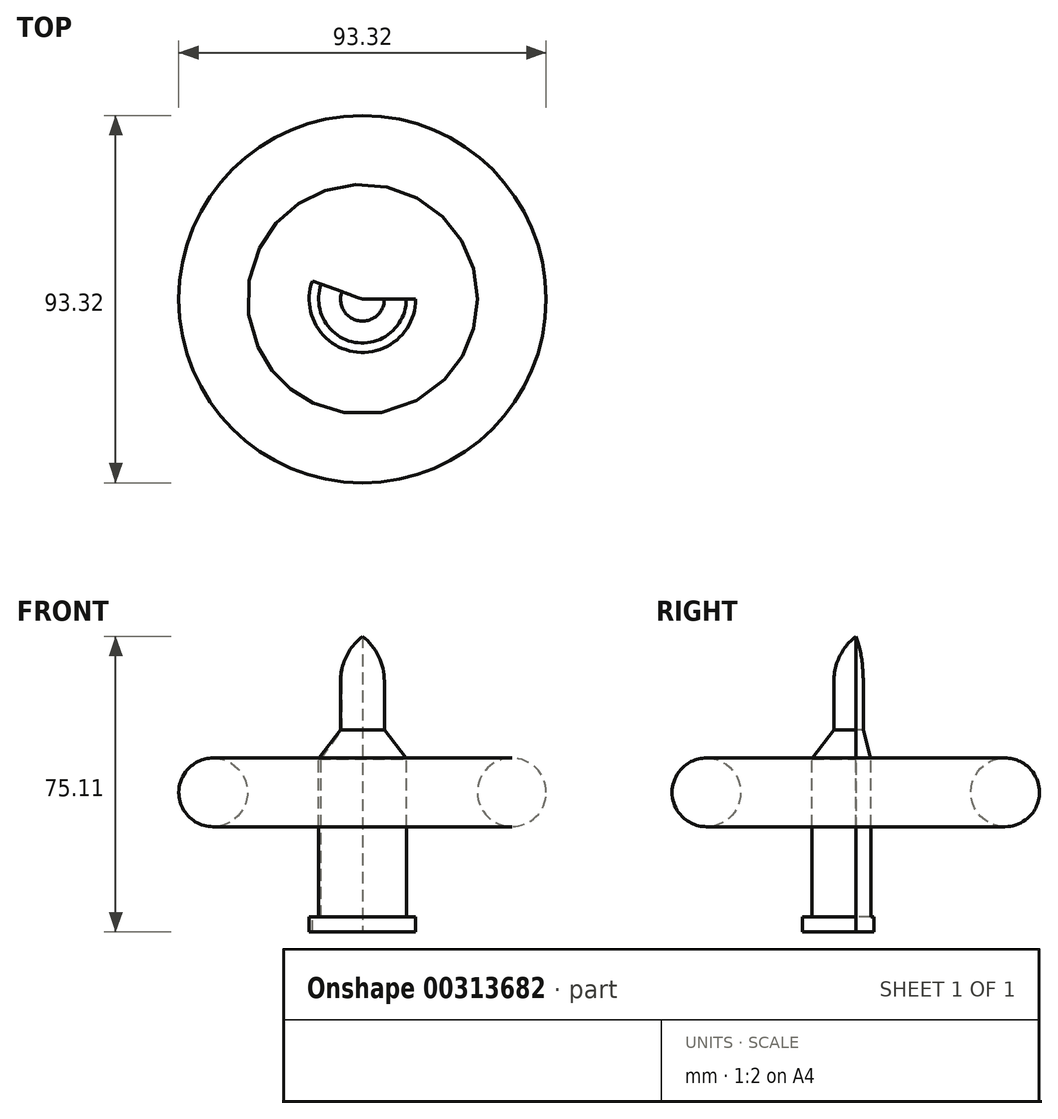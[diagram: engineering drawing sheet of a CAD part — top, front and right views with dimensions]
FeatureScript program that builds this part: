
annotation { "Feature Type Name" : "Feature", "Feature Type Description" : "" }
export const myFeature = defineFeature(function(context is Context, id is Id, definition is map)
    precondition{}
    {
        {
            var Q0;
            Q0=qCreatedBy(makeId("Front.planeOp"),FACE);
            var sketch = newSketch(context, id + "F0", { "sketchPlane" : qUnion([Q0])});
            skLineSegment(sketch, "E0", {"start": v(0, 0) * mm, "end": v(13.53, 0) * mm});
            skLineSegment(sketch, "E1", {"start": v(13.53, 0) * mm, "end": v(13.53, 3.8) * mm});
            skLineSegment(sketch, "E2", {"start": v(11.13, 3.8) * mm, "end": v(11.13, 44.02) * mm});
            skLineSegment(sketch, "E3", {"start": v(11.13, 44.02) * mm, "end": v(5.56, 51.32) * mm});
            skLineSegment(sketch, "E4", {"start": v(5.56, 51.32) * mm, "end": v(5.56, 63.68) * mm});
            skArc(sketch, "E5", {"start": v(5.56, 63.68) * mm, "mid": v(4.1, 70.04) * mm, "end": v(0, 75.11) * mm});
            skLineSegment(sketch, "E6", {"start": v(0, 75.11) * mm, "end": v(0, 0) * mm});
            skLineSegment(sketch, "E7", {"start": v(13.53, 3.8) * mm, "end": v(11.13, 3.8) * mm});
            skSolve(sketch);
        }
        {
            var Q0;
            Q0=makeQuery(id+"F0.imprint","IMPRINT",FACE,{"disambiguationData":[TD([[makeQuery(id+"F0.imprint","IMPRINT",EDGE,{"derivedFrom":sQuery(id+"F0.wireOp",EDGE,"E0")}),1.0]])]});
            var Q1;
            Q1=sQuery(id+"F0.wireOp",EDGE,"E6");
            revolve(context, id + "F1", {"entities" : qUnion([Q0]), "axis" : qUnion([Q1]), "revolveType" : RevolveType.ONE_DIRECTION, "angle" : 200 * degree});
        }
        {
            var Q0;
            Q0=qCreatedBy(makeId("Front.planeOp"),FACE);
            var sketch = newSketch(context, id + "F2", { "sketchPlane" : qUnion([Q0])});
            skCircle(sketch, "E8", {"center": v(37.94, 35.47) * mm, "radius": 8.72 * mm});
            skLineSegment(sketch, "E9.0", {"start": v(0, 75.11) * mm, "end": v(0, 0) * mm});
            skSolve(sketch);
        }
        {
            var Q0;
            Q0=makeQuery(id+"F2.imprint","IMPRINT",FACE,{"disambiguationData":[TD([[makeQuery(id+"F2.imprint","IMPRINT",EDGE,{"derivedFrom":sQuery(id+"F2.wireOp",EDGE,"E8")}),1.0]])]});
            var Q1;
            Q1=sQuery(id+"F2.wireOp",EDGE,"E9.0");
            revolve(context, id + "F3", {"entities" : qUnion([Q0]), "axis" : qUnion([Q1]), "revolveType" : RevolveType.FULL});
        }
    });
